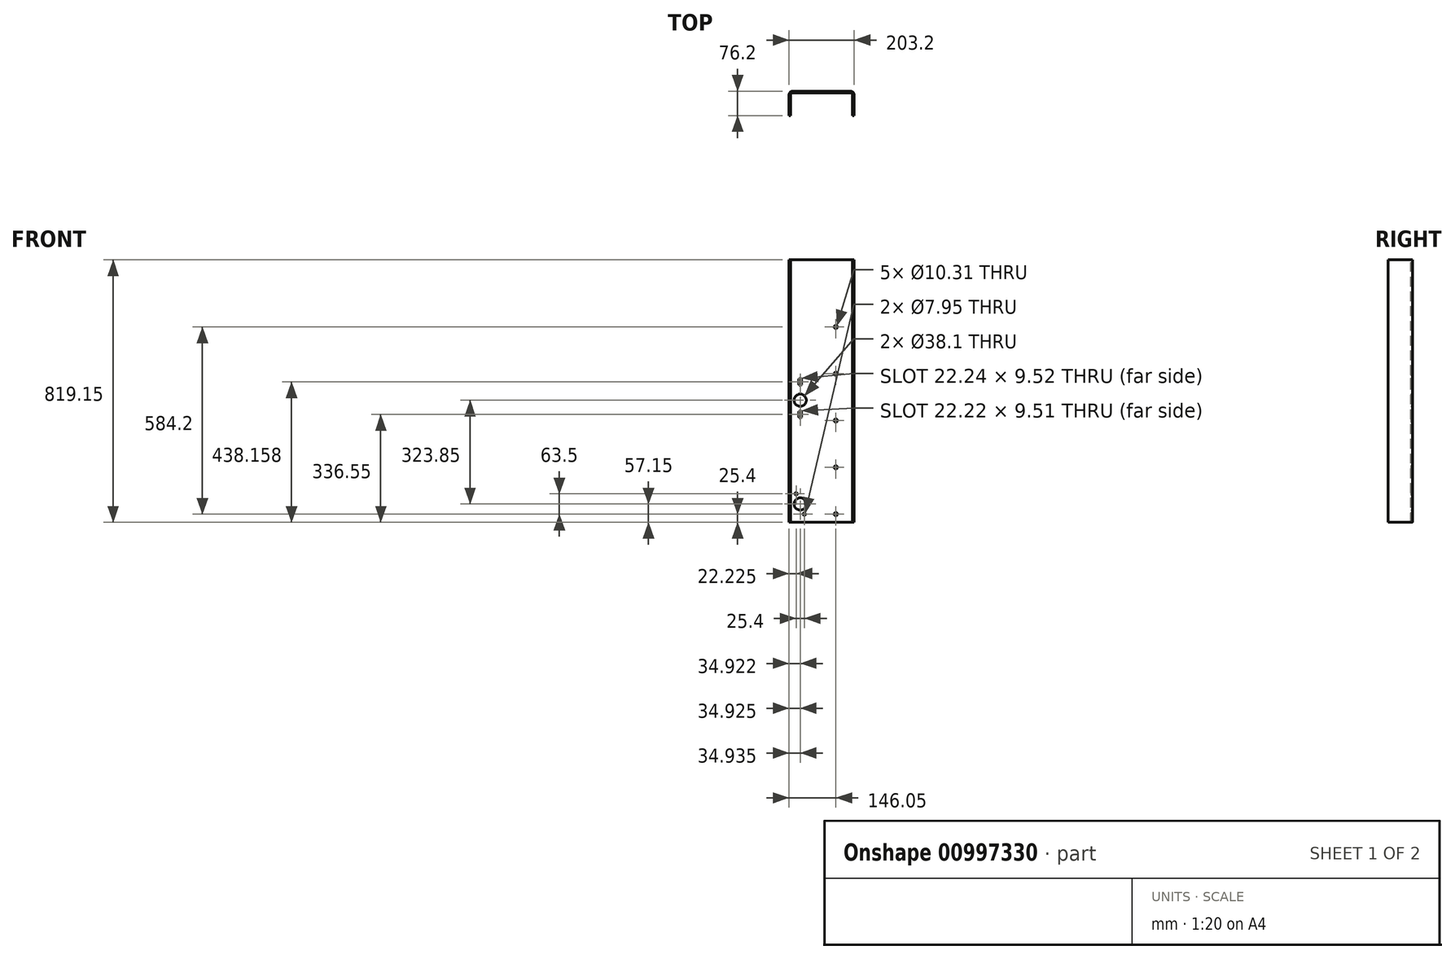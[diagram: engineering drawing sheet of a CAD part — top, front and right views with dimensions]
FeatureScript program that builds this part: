
annotation { "Feature Type Name" : "Feature", "Feature Type Description" : "" }
export const myFeature = defineFeature(function(context is Context, id is Id, definition is map)
    precondition{}
    {
        {
            var Q0;
            Q0=qCreatedBy(makeId("Top.planeOp"),FACE);
            var sketch = newSketch(context, id + "F0", { "sketchPlane" : qUnion([Q0])});
            skLineSegment(sketch, "E0.bottom", {"start": v(90.47, 38.1) * mm, "end": v(-90.47, 38.1) * mm});
            skLineSegment(sketch, "E0.top", {"start": v(101.6, -38.1) * mm, "end": v(96.82, -38.1) * mm});
            skLineSegment(sketch, "E0.left", {"start": v(101.6, 26.97) * mm, "end": v(101.6, -38.1) * mm});
            skLineSegment(sketch, "E0.right", {"start": v(-101.6, 26.97) * mm, "end": v(-101.6, -38.1) * mm});
            skPoint(sketch, "E0.middle", {"position": v(0, 0) * mm});
            skLineSegment(sketch, "E1.0", {"start": v(90.47, 33.32) * mm, "end": v(-90.47, 33.32) * mm});
            skLineSegment(sketch, "E2.0", {"start": v(-96.82, 26.97) * mm, "end": v(-96.82, -38.1) * mm});
            skLineSegment(sketch, "E3.0", {"start": v(96.82, 26.97) * mm, "end": v(96.82, -38.1) * mm});
            skArc(sketch, "E4.filletArc", {"start": v(-90.47, 33.32) * mm, "mid": v(-94.96, 31.46) * mm, "end": v(-96.82, 26.97) * mm});
            skArc(sketch, "E5.filletArc", {"start": v(96.82, 26.97) * mm, "mid": v(94.96, 31.46) * mm, "end": v(90.47, 33.32) * mm});
            skArc(sketch, "E6.0", {"start": v(-90.47, 38.1) * mm, "mid": v(-98.34, 34.84) * mm, "end": v(-101.6, 26.97) * mm});
            skArc(sketch, "E7.0", {"start": v(101.6, 26.97) * mm, "mid": v(98.34, 34.84) * mm, "end": v(90.47, 38.1) * mm});
            skPoint(sketch, "E8.orphan", {"position": v(-101.6, 38.1) * mm});
            skPoint(sketch, "E9.orphan", {"position": v(101.6, 38.1) * mm});
            skLineSegment(sketch, "E10.trimOffspring", {"start": v(-96.82, -38.1) * mm, "end": v(-101.6, -38.1) * mm});
            skSolve(sketch);
        }
        {
            var Q0;
            Q0=makeQuery(id+"F0.imprint","IMPRINT",FACE,{"disambiguationData":[TD([[makeQuery(id+"F0.imprint","IMPRINT",EDGE,{"derivedFrom":sQuery(id+"F0.wireOp",EDGE,"E0.bottom")}),1.0]])]});
            extrude(context, id + "F1", {"entities" : qUnion([Q0]), "oppositeDirection" : true, "depth" : 819.15 * mm, "offsetDistance" : 25.4 * mm});
        }
        {
            var Q0;
            Q0=makeQuery(id+"F1.opExtrude","SWEPT_FACE",FACE,{"disambiguationData":[OSD([sQuery(id+"F0.wireOp",EDGE,"E0.bottom")])]});
            var sketch = newSketch(context, id + "F2", { "sketchPlane" : qUnion([Q0])});
            skLineSegment(sketch, "E11", {"start": v(0, -819.15) * mm, "end": v(0, 0) * mm, "construction": true});
            skLineSegment(sketch, "E12.0", {"start": v(-44.45, -819.15) * mm, "end": v(-44.45, 0) * mm, "construction": true});
            skLineSegment(sketch, "E13.0", {"start": v(66.68, -819.15) * mm, "end": v(66.68, 0) * mm, "construction": true});
            skCircle(sketch, "E14", {"center": v(-44.45, -209.55) * mm, "radius": 5.16 * mm});
            skCircle(sketch, "E15", {"center": v(-44.45, -355.6) * mm, "radius": 5.16 * mm});
            skCircle(sketch, "E16", {"center": v(-44.45, -501.65) * mm, "radius": 5.16 * mm});
            skCircle(sketch, "E17", {"center": v(-44.45, -647.7) * mm, "radius": 5.16 * mm});
            skCircle(sketch, "E18", {"center": v(-44.45, -793.75) * mm, "radius": 5.16 * mm});
            skCircle(sketch, "E19", {"center": v(66.68, -438.15) * mm, "radius": 19.05 * mm});
            skCircle(sketch, "E20", {"center": v(66.68, -762) * mm, "radius": 19.05 * mm});
            skArc(sketch, "E21", {"start": v(71.43, -374.24) * mm, "mid": v(66.24, -369.9) * mm, "end": v(61.92, -375.1) * mm});
            skArc(sketch, "E22", {"start": v(61.92, -387.12) * mm, "mid": v(66.56, -392.11) * mm, "end": v(71.44, -387.35) * mm});
            skArc(sketch, "E23", {"start": v(71.42, -476.68) * mm, "mid": v(66.9, -471.5) * mm, "end": v(61.91, -476.25) * mm});
            skArc(sketch, "E24", {"start": v(61.91, -488.95) * mm, "mid": v(66.9, -493.7) * mm, "end": v(71.42, -488.52) * mm});
            skLineSegment(sketch, "E25", {"start": v(71.43, -374.24) * mm, "end": v(71.44, -387.35) * mm});
            skLineSegment(sketch, "E26", {"start": v(61.92, -374.2) * mm, "end": v(61.92, -387.58) * mm});
            skLineSegment(sketch, "E27", {"start": v(61.91, -476.25) * mm, "end": v(61.91, -488.95) * mm});
            skLineSegment(sketch, "E28", {"start": v(71.42, -489.38) * mm, "end": v(71.42, -476.68) * mm});
            skPoint(sketch, "E29", {"position": v(71.42, -483.03) * mm});
            skPoint(sketch, "E30", {"position": v(71.44, -380.8) * mm});
            skCircle(sketch, "E31", {"center": v(79.38, -730.25) * mm, "radius": 3.98 * mm});
            skCircle(sketch, "E32", {"center": v(53.98, -793.75) * mm, "radius": 3.98 * mm});
            skSolve(sketch);
        }
        {
            var Q0;
            Q0=makeQuery(id+"F2.imprint","IMPRINT",FACE,{"disambiguationData":[TD([[makeQuery(id+"F2.imprint","IMPRINT",EDGE,{"derivedFrom":sQuery(id+"F2.wireOp",EDGE,"E14")}),1.0]])]});
            var Q1;
            Q1=makeQuery(id+"F2.imprint","IMPRINT",FACE,{"disambiguationData":[TD([[makeQuery(id+"F2.imprint","IMPRINT",EDGE,{"derivedFrom":sQuery(id+"F2.wireOp",EDGE,"E15")}),1.0]])]});
            var Q2;
            Q2=makeQuery(id+"F2.imprint","IMPRINT",FACE,{"disambiguationData":[TD([[makeQuery(id+"F2.imprint","IMPRINT",EDGE,{"derivedFrom":sQuery(id+"F2.wireOp",EDGE,"E16")}),1.0]])]});
            var Q3;
            Q3=makeQuery(id+"F2.imprint","IMPRINT",FACE,{"disambiguationData":[TD([[makeQuery(id+"F2.imprint","IMPRINT",EDGE,{"derivedFrom":sQuery(id+"F2.wireOp",EDGE,"E17")}),1.0]])]});
            var Q4;
            Q4=makeQuery(id+"F2.imprint","IMPRINT",FACE,{"disambiguationData":[TD([[makeQuery(id+"F2.imprint","IMPRINT",EDGE,{"derivedFrom":sQuery(id+"F2.wireOp",EDGE,"E18")}),1.0]])]});
            var Q5;
            Q5=makeQuery(id+"F2.imprint","IMPRINT",FACE,{"disambiguationData":[TD([[makeQuery(id+"F2.imprint","IMPRINT",EDGE,{"derivedFrom":sQuery(id+"F2.wireOp",EDGE,"E32")}),1.0]])]});
            var Q6;
            Q6=makeQuery(id+"F2.imprint","IMPRINT",FACE,{"disambiguationData":[TD([[makeQuery(id+"F2.imprint","IMPRINT",EDGE,{"derivedFrom":sQuery(id+"F2.wireOp",EDGE,"E20")}),1.0]])]});
            var Q7;
            Q7=makeQuery(id+"F2.imprint","IMPRINT",FACE,{"disambiguationData":[TD([[makeQuery(id+"F2.imprint","IMPRINT",EDGE,{"derivedFrom":sQuery(id+"F2.wireOp",EDGE,"E31")}),1.0]])]});
            var Q8;
            Q8=makeQuery(id+"F2.imprint","IMPRINT",FACE,{"disambiguationData":[TD([[makeQuery(id+"F2.imprint","IMPRINT",EDGE,{"derivedFrom":sQuery(id+"F2.wireOp",EDGE,"E19")}),1.0]])]});
            var Q9;
            {var subQ5=sQuery(id+"F2.wireOp",EDGE,"E23");Q9=makeQuery(id+"F2.imprint","IMPRINT",FACE,{"disambiguationData":[TD([[makeQuery(id+"F2.imprint","IMPRINT",EDGE,{"derivedFrom":subQ5}),1.0]])]});}
            var Q10;
            {var subQ0=sQuery(id+"F2.wireOp",EDGE,"E25");Q10=makeQuery(id+"F2.imprint","IMPRINT",FACE,{"disambiguationData":[TD([[makeQuery(id+"F2.imprint","IMPRINT",EDGE,{"derivedFrom":subQ0}),-1.0]])]});}
            extrude(context, id + "F3", {"entities" : qUnion([Q0, Q1, Q2, Q3, Q4, Q5, Q6, Q7, Q8, Q9, Q10]), "operationType" : NewBodyOperationType.REMOVE, "endBound" : BoundingType.THROUGH_ALL, "oppositeDirection" : true, "depth" : 25.4 * mm, "offsetDistance" : 25.4 * mm});
        }
    });
